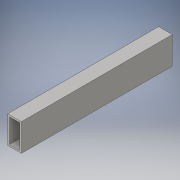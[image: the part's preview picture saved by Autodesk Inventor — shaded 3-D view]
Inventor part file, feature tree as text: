
AUTODESK INVENTOR PART (.ipt)
format: ipt  version: 2016 (Build 200138000, 138)  size: 92,160 bytes
history: native  units: in
note: dims shown in document units (in); Inventor stores cm internally (conversion verified against a paired STEP export)
features: extrude x1, shell x1, sketch x1
ambient origin geometry x8: Origin, YZ Plane, XZ Plane, XY Plane, X Axis, Y Axis, Z Axis, Center Point
bodies: Solid1 (feature_tree)
feature tree (3):
  extrude  "Extrusion1"  Depth=2.0in
  shell  "Shell1"  Thickness=11.0in
  sketch  "Sketch1"  dims[d0=1.0in d1=2.0in d2=11.0in d3=0.0in d4=0.125in]
